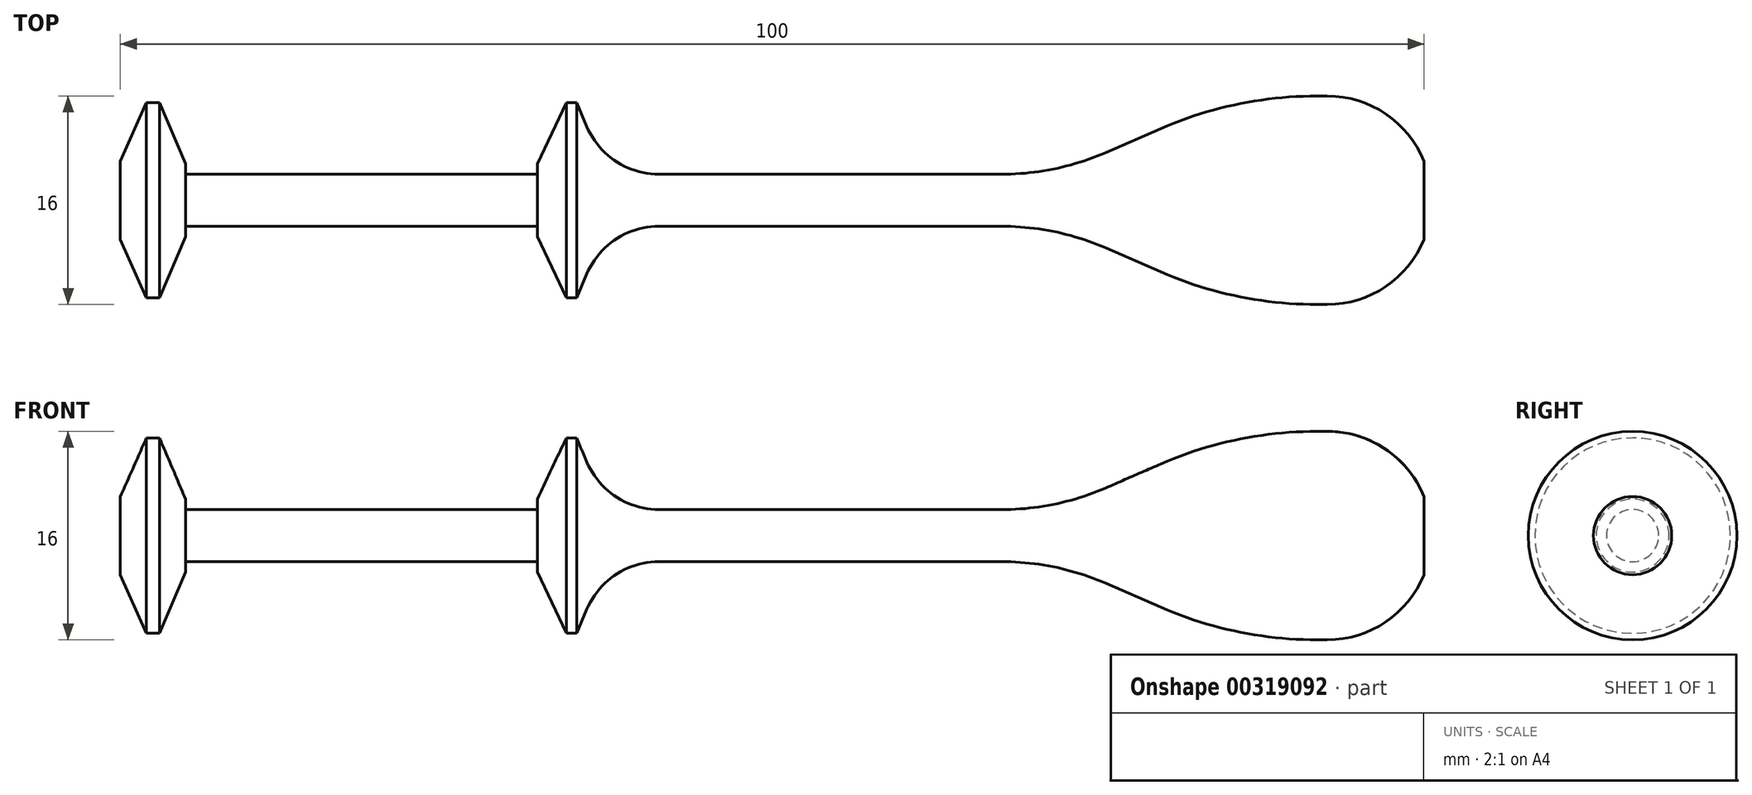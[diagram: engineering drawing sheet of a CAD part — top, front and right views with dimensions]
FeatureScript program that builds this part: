
annotation { "Feature Type Name" : "Feature", "Feature Type Description" : "" }
export const myFeature = defineFeature(function(context is Context, id is Id, definition is map)
    precondition{}
    {
        {
            var Q0;
            Q0=qCreatedBy(makeId("Front.planeOp"),FACE);
            var sketch = newSketch(context, id + "F0", { "sketchPlane" : qUnion([Q0])});
            skLineSegment(sketch, "E0", {"start": v(5, 2) * mm, "end": v(32, 2) * mm});
            skLineSegment(sketch, "E1", {"start": v(32, 2) * mm, "end": v(32, 2) * mm});
            skLineSegment(sketch, "E2", {"start": v(32, 2.8) * mm, "end": v(32, 2) * mm});
            skLineSegment(sketch, "E3", {"start": v(5, 2.8) * mm, "end": v(5, 2) * mm});
            skLineSegment(sketch, "E4", {"start": v(34.2, 7.5) * mm, "end": v(35, 7.5) * mm});
            skLineSegment(sketch, "E5", {"start": v(27.34, 5.9) * mm, "end": v(27.34, 5.9) * mm});
            skLineSegment(sketch, "E6", {"start": v(41.3, 2) * mm, "end": v(67.6, 2) * mm});
            skLineSegment(sketch, "E7", {"start": v(90.1, 2) * mm, "end": v(90.1, 2) * mm});
            skLineSegment(sketch, "E8", {"start": v(100, 3) * mm, "end": v(100, 0) * mm});
            skLineSegment(sketch, "E9", {"start": v(100, 0) * mm, "end": v(100, 0) * mm});
            skLineSegment(sketch, "E10", {"start": v(3, 7.5) * mm, "end": v(2, 7.5) * mm});
            skLineSegment(sketch, "E11", {"start": v(0, 3) * mm, "end": v(0, 0) * mm});
            skLineSegment(sketch, "E12", {"start": v(0, 0) * mm, "end": v(100, 0) * mm});
            skLineSegment(sketch, "E13", {"start": v(2, 7.5) * mm, "end": v(0, 3) * mm});
            skLineSegment(sketch, "E14", {"start": v(3, 7.5) * mm, "end": v(5, 2.8) * mm});
            skLineSegment(sketch, "E15", {"start": v(32, 2.8) * mm, "end": v(34.2, 7.5) * mm});
            skLineSegment(sketch, "E16", {"start": v(35, 7.5) * mm, "end": v(35.78, 5.66) * mm});
            skArc(sketch, "E17.filletArc", {"start": v(35.78, 5.66) * mm, "mid": v(38, 3) * mm, "end": v(41.3, 2) * mm});
            skLineSegment(sketch, "E18", {"start": v(91.8, 8) * mm, "end": v(92.58, 8) * mm});
            skLineSegment(sketch, "E19", {"start": v(79.82, 5.5) * mm, "end": v(75.59, 3.66) * mm});
            skArc(sketch, "E20.filletArc", {"start": v(91.8, 8) * mm, "mid": v(85.68, 7.37) * mm, "end": v(79.82, 5.5) * mm});
            skArc(sketch, "E21.filletArc", {"start": v(67.6, 2) * mm, "mid": v(71.68, 2.42) * mm, "end": v(75.59, 3.66) * mm});
            skArc(sketch, "E22", {"start": v(100, 3) * mm, "mid": v(97.06, 6.63) * mm, "end": v(92.58, 8) * mm});
            skSolve(sketch);
        }
        {
            var Q0;
            Q0=qCreatedBy(makeId("Front.planeOp"),FACE);
            var sketch = newSketch(context, id + "F1", { "sketchPlane" : qUnion([Q0])});
            skLineSegment(sketch, "E23", {"start": v(0, 0) * mm, "end": v(66.73, 0) * mm, "construction": true});
            skSolve(sketch);
        }
        {
            var Q0;
            Q0 = qSketchRegion(id + "F0", true);
            var Q1;
            Q1 = qBodyType(qCreatedBy(id + "F1" ,EDGE), BodyType.WIRE);
            revolve(context, id + "F2", {"entities" : qUnion([Q0]), "axis" : qUnion([Q1]), "revolveType" : RevolveType.FULL});
        }
    });
